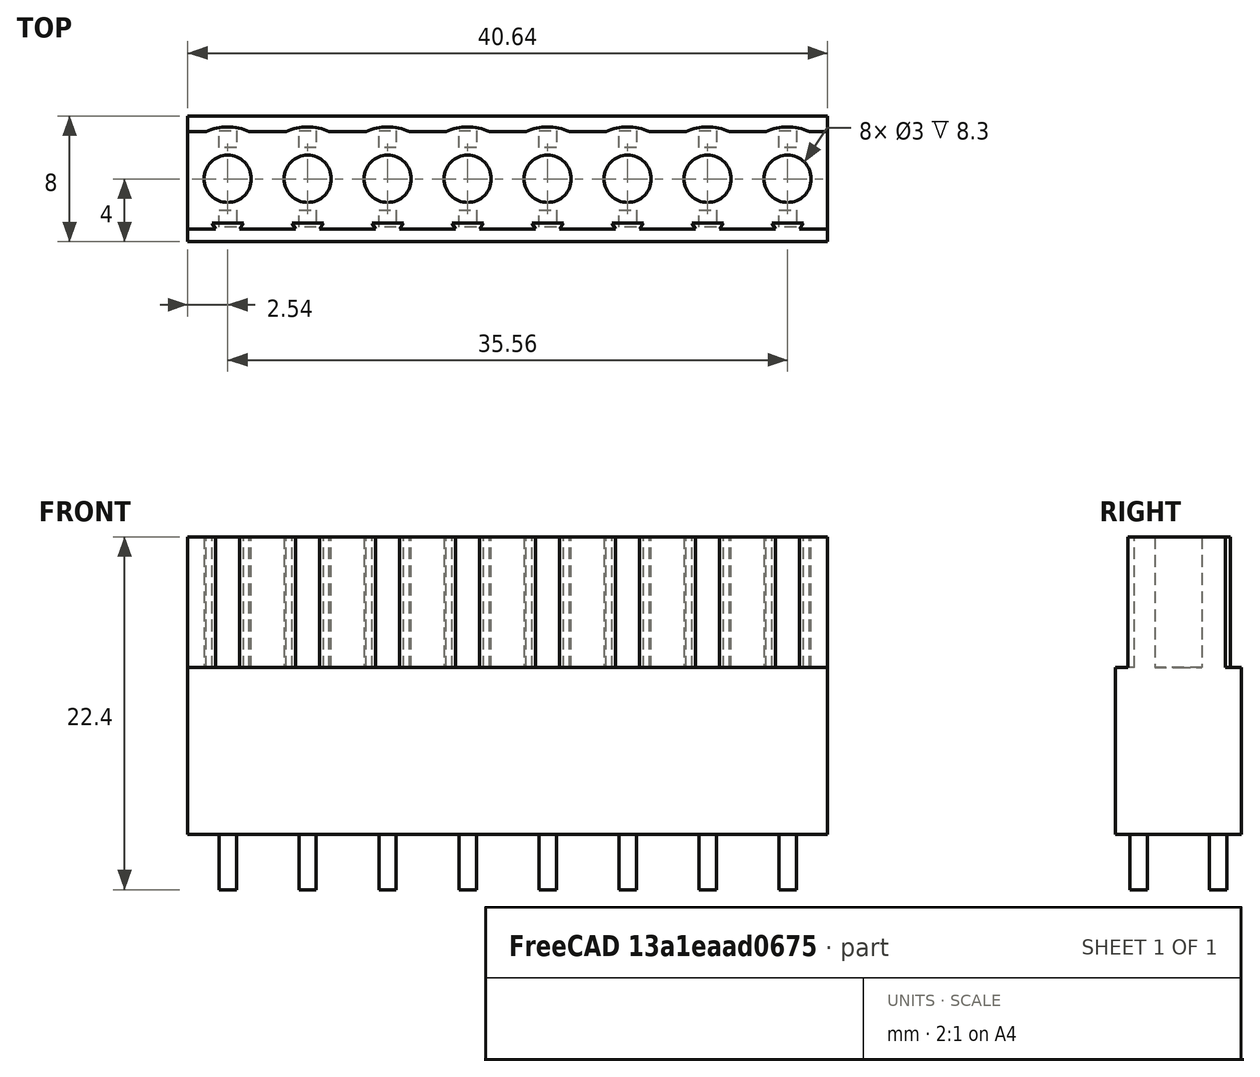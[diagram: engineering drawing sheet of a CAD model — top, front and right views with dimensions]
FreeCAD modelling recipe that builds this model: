
FCSTD DOCUMENT  (FreeCAD 1.1R44227 +647 (Git))
Label: 950066008000000
License: All rights reserved
objects: Sketcher::SketchObject×3, PartDesign::Pad×3, App::Point×1, PartDesign::Body×1, PartDesign::LinearPattern×1
note: 18 computed .brp shape members not serialized (recipe doc carries the construction recipe); baked Part::Feature solids carry a one-line shape summary decoded from their .brp

FEATURE [App::Point] Origin001
  Role = Origin
FEATURE [Sketcher::SketchObject] Sketch
  ArcFitTolerance = 1e-06
  AttachmentSupport = -> [Origin]
  ExternalTypes = [0]
  FullyConstrained = true
  MakeInternals = false
  MapMode = 5
  _ExternalGeoVersion = 1
  sketch-geometry (4):
    g0: LineSegment StartX=-2.54 StartY=4 StartZ=0 EndX=-2.54 EndY=-4 EndZ=0
    g1: LineSegment StartX=-2.54 StartY=-4 StartZ=0 EndX=38.1 EndY=-4 EndZ=0
    g2: LineSegment StartX=38.1 StartY=-4 StartZ=0 EndX=38.1 EndY=4 EndZ=0
    g3: LineSegment StartX=38.1 StartY=4 StartZ=0 EndX=-2.54 EndY=4 EndZ=0
  constraints (12):
    c: Coincident(g0,g1)
    c: Coincident(g1,g2)
    c: Coincident(g2,g3)
    c: Coincident(g3,g0)
    c: Vertical(g0)
    c: Vertical(g2)
    c: Horizontal(g1)
    c: Horizontal(g3)
    c: Distance(g0,g0) = 8
    c: DistanceY(g-1,g0) = 4
    c: DistanceX(g3,g3) = 40.64
    c: DistanceX(g0,g-1) = 2.54
FEATURE [PartDesign::Pad] Pad
  Direction = (0,0,1)
  Length = 10.6
  Length2 = 10
  Profile = -> Sketch
  ReferenceAxis = -> Sketch [N_Axis]
  Refine = true
  SideType = 0
  Suppressed = false
  Type = 0
  Type2 = 0
FEATURE [Sketcher::SketchObject] Sketch001
  ArcFitTolerance = 1e-06
  AttachmentSupport = -> [Pad]
  ExternalTypes = [0]
  FullyConstrained = true
  MakeInternals = false
  MapMode = 5
  Placement = pos=(0,0,10.6) rot=(0,0,1;0rad)
  _ExternalGeoVersion = 1
  sketch-geometry (18):
    g0: Circle CenterX=0 CenterY=0 CenterZ=0 NormalX=0 NormalY=0 NormalZ=1 AngleXU=0 Radius=1.5
    g1: ArcOfCircle CenterX=0 CenterY=0 CenterZ=0 NormalX=0 NormalY=0 NormalZ=1 AngleXU=0 Radius=3.3 StartAngle=1.1411 EndAngle=2.0005
    g2: LineSegment StartX=-1.37477 StartY=3 StartZ=0 EndX=-2.54 EndY=3 EndZ=0
    g3: LineSegment StartX=1.37477 StartY=3 StartZ=0 EndX=2.54 EndY=3 EndZ=0
    g4: LineSegment [constr] StartX=-1.37477 StartY=3 StartZ=0 EndX=1.37477 EndY=3 EndZ=0
    g5: LineSegment StartX=2.54 StartY=3 StartZ=0 EndX=2.54 EndY=-3.2 EndZ=0
    g6: LineSegment StartX=2.54 StartY=-3.2 StartZ=0 EndX=0.76906 EndY=-3.2 EndZ=0
    g7: LineSegment StartX=-2.54 StartY=-3.2 StartZ=0 EndX=-2.54 EndY=3 EndZ=0
    g8: LineSegment [constr] StartX=0 StartY=0 StartZ=0 EndX=2.54 EndY=3 EndZ=0
    g9: LineSegment [constr] StartX=0 StartY=0 StartZ=0 EndX=-2.54 EndY=3 EndZ=0
    g10: LineSegment StartX=-0.76906 StartY=-3.2 StartZ=0 EndX=-2.54 EndY=-3.2 EndZ=0
    g11: LineSegment StartX=-0.76906 StartY=-3.2 StartZ=0 EndX=-1 EndY=-2.8 EndZ=0
    g12: LineSegment StartX=-1 StartY=-2.8 StartZ=0 EndX=1 EndY=-2.8 EndZ=0
    g13: LineSegment StartX=1 StartY=-2.8 StartZ=0 EndX=0.76906 EndY=-3.2 EndZ=0
    g14: LineSegment [constr] StartX=-0.76906 StartY=-3.2 StartZ=0 EndX=0.76906 EndY=-3.2 EndZ=0
    g15: LineSegment [constr] StartX=-0.76906 StartY=-3.2 StartZ=0 EndX=1 EndY=-2.8 EndZ=0
    g16: LineSegment [constr] StartX=-1 StartY=-2.8 StartZ=0 EndX=0.76906 EndY=-3.2 EndZ=0
    g17: GeomPoint [constr] X=0 Y=-3.2 Z=0
  constraints (45):
    c: Coincident(g0,g-1)
    c: Diameter(g0) = 3
    c: Coincident(g1,g0)
    c: Coincident(g2,g1)
    c: Horizontal(g2)
    c: Coincident(g3,g1)
    c: Horizontal(g3)
    c: Coincident(g4,g1)
    c: Coincident(g4,g1)
    c: Horizontal(g4)
    c: Coincident(g5,g3)
    c: Vertical(g5)
    c: Coincident(g6,g5)
    c: Coincident(g7,g10)
    c: Coincident(g7,g2)
    c: Vertical(g7)
    c: Coincident(g8,g0)
    c: Coincident(g8,g3)
    c: Coincident(g9,g0)
    c: Coincident(g9,g2)
    c: Equal(g9,g8)
    c: Distance(g6,g10) = 5.08
    c: Radius(g1) = 3.3
    c: DistanceY(g-1,g2) = 3
    c: DistanceY(g7,g7) = 6.2
    c: Horizontal(g6)
    c: Horizontal(g10)
    c: Coincident(g11,g10)
    c: Coincident(g12,g11)
    c: Horizontal(g12)
    c: Coincident(g13,g12)
    c: Coincident(g13,g6)
    c: Coincident(g14,g10)
    c: Coincident(g14,g6)
    c: Horizontal(g14)
    c: Coincident(g15,g10)
    c: Coincident(g15,g12)
    c: Coincident(g16,g11)
    c: Coincident(g16,g6)
    c: Equal(g15,g16)
    c: Angle(g11,g10) = 1.0472
    c: DistanceX(g12,g12) = 2
    c: DistanceY(g6,g12) = 0.4
    c: Symmetric(g14,g14,g17)
    c: PointOnObject(g17,g-2)
FEATURE [PartDesign::Pad] Pad001
  BaseFeature = -> Pad
  Direction = (0,0,1)
  Length = 8.3
  Length2 = 10
  Profile = -> Sketch001
  ReferenceAxis = -> Sketch001 [N_Axis]
  Refine = true
  SideType = 0
  Suppressed = false
  Type = 0
  Type2 = 0
FEATURE [PartDesign::Body] Body
  AllowCompound = false
  Group = -> [Sketch,Pad,Sketch001,Pad001,LinearPattern,Sketch002,Pad002]
  Origin = -> Origin
  Tip = -> Pad002
FEATURE [PartDesign::LinearPattern] LinearPattern
  BaseFeature = -> Pad001
  Direction = -> Sketch001 [H_Axis]
  Direction2 = -> Sketch001 [V_Axis]
  Length = 35.56
  Length2 = 100
  Mode = 0
  Mode2 = 0
  Occurrences = 8
  Occurrences2 = 1
  Offset = 5.08
  Offset2 = 100
  Originals = -> [Pad001,Pad002]
  Refine = true
  Reversed2 = false
  SpacingPattern = [0]
  SpacingPattern2 = [0]
  Spacings = [-1,-1,-1,-1,-1,-1,-1]
  Suppressed = false
  TransformMode = 0
FEATURE [Sketcher::SketchObject] Sketch002
  ArcFitTolerance = 1e-06
  AttachmentSupport = -> [LinearPattern]
  ExternalGeometry = -> [LinearPattern]
  ExternalTypes = [0]
  FullyConstrained = true
  MakeInternals = false
  MapMode = 5
  Placement = pos=(0,0,0) rot=(1,0,0;3.14159rad)
  _ExternalGeoVersion = 1
  sketch-geometry (10):
    g0: LineSegment StartX=-0.55 StartY=3.07 StartZ=0 EndX=-0.55 EndY=1.97 EndZ=0
    g1: LineSegment StartX=-0.55 StartY=1.97 StartZ=0 EndX=0.55 EndY=1.97 EndZ=0
    g2: LineSegment StartX=0.55 StartY=1.97 StartZ=0 EndX=0.55 EndY=3.07 EndZ=0
    g3: LineSegment StartX=0.55 StartY=3.07 StartZ=0 EndX=-0.55 EndY=3.07 EndZ=0
    g4: GeomPoint [constr] X=0 Y=2.52 Z=0
    g5: LineSegment StartX=-0.55 StartY=-1.97 StartZ=0 EndX=-0.55 EndY=-3.07 EndZ=0
    g6: LineSegment StartX=-0.55 StartY=-3.07 StartZ=0 EndX=0.55 EndY=-3.07 EndZ=0
    g7: LineSegment StartX=0.55 StartY=-3.07 StartZ=0 EndX=0.55 EndY=-1.97 EndZ=0
    g8: LineSegment StartX=0.55 StartY=-1.97 StartZ=0 EndX=-0.55 EndY=-1.97 EndZ=0
    g9: GeomPoint [constr] X=0 Y=-2.52 Z=0
  constraints (26):
    c: Coincident(g0,g1)
    c: Coincident(g1,g2)
    c: Coincident(g2,g3)
    c: Coincident(g3,g0)
    c: Vertical(g0)
    c: Vertical(g2)
    c: Horizontal(g1)
    c: Horizontal(g3)
    c: Symmetric(g2,g0,g4)
    c: PointOnObject(g4,g-2)
    c: Coincident(g5,g6)
    c: Coincident(g6,g7)
    c: Coincident(g7,g8)
    c: Coincident(g8,g5)
    c: Vertical(g5)
    c: Vertical(g7)
    c: Horizontal(g6)
    c: Horizontal(g8)
    c: Symmetric(g7,g5,g9)
    c: PointOnObject(g9,g-2)
    c: Equal(g2,g3)
    c: Equal(g3,g8)
    c: Equal(g8,g7)
    c: Distance(g7,g7) = 1.1
    c: DistanceY(g9,g4) = 5.04
    c: DistanceY(g-6,g9) = 1.48
FEATURE [PartDesign::Pad] Pad002
  BaseFeature = -> LinearPattern
  Direction = (0,0,-1)
  Length = 3.5
  Length2 = 10
  Profile = -> Sketch002
  ReferenceAxis = -> Sketch002 [N_Axis]
  Refine = true
  SideType = 0
  Suppressed = false
  Type = 0
  Type2 = 0
